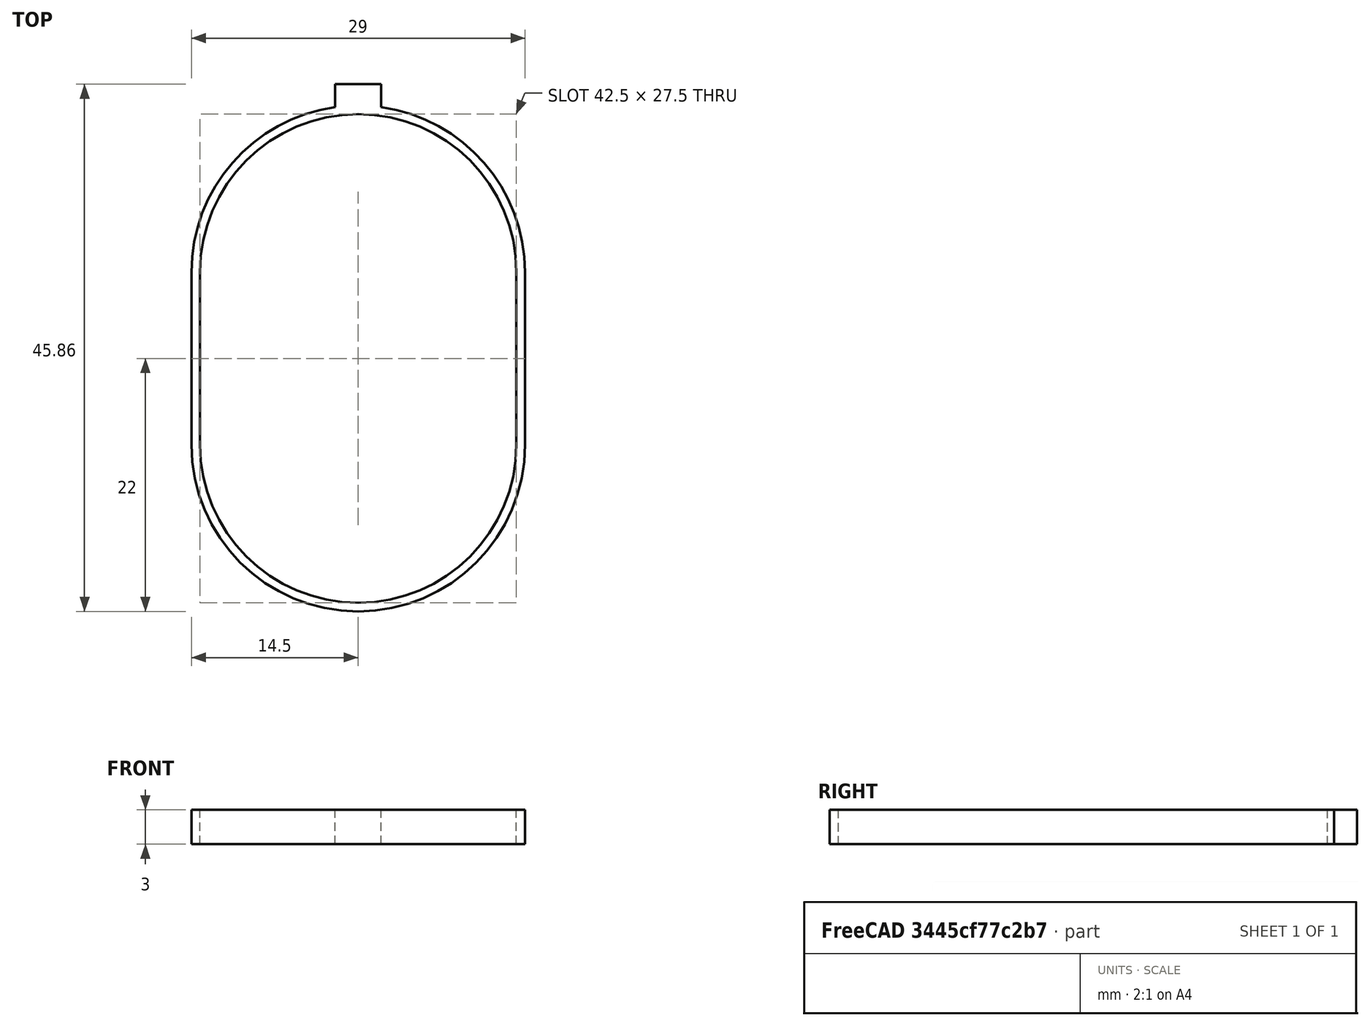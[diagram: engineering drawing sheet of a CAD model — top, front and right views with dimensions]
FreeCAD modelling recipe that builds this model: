
FCSTD DOCUMENT  (FreeCAD 0.19R)
Label: OTS-0005-00_zip-tie
License: All rights reserved
LicenseURL: http://en.wikipedia.org/wiki/All_rights_reserved
objects: Sketcher::SketchObject×1, PartDesign::Pad×1, PartDesign::Body×1
note: 4 computed .brp shape members not serialized (recipe doc carries the construction recipe); baked Part::Feature solids carry a one-line shape summary decoded from their .brp

FEATURE [Sketcher::SketchObject] Sketch
  FullyConstrained = true
  MapMode = 5
  Support = -> [XY_Plane]
  sketch-geometry (12):
    g0: ArcOfCircle CenterX=0 CenterY=-14.5 CenterZ=0 NormalX=0 NormalY=0 NormalZ=1 AngleXU=0 Radius=14.5 StartAngle=1.70917 EndAngle=3.14159
    g1: LineSegment StartX=2 StartY=-0.138593 StartZ=0 EndX=2 EndY=1.86141 EndZ=0
    g2: LineSegment StartX=2 StartY=1.86141 StartZ=0 EndX=-2 EndY=1.86141 EndZ=0
    g3: LineSegment StartX=-2 StartY=1.86141 StartZ=0 EndX=-2 EndY=-0.138593 EndZ=0
    g4: ArcOfCircle CenterX=0 CenterY=-14.5 CenterZ=0 NormalX=0 NormalY=0 NormalZ=1 AngleXU=0 Radius=13.75 StartAngle=7.87486e-07 EndAngle=3.14159
    g5: ArcOfCircle CenterX=0 CenterY=-14.5 CenterZ=0 NormalX=0 NormalY=0 NormalZ=1 AngleXU=0 Radius=14.5 StartAngle=2.61187e-06 EndAngle=1.43242
    g6: LineSegment StartX=-14.5 StartY=-14.5 StartZ=0 EndX=-14.5 EndY=-29.5 EndZ=0
    g7: LineSegment StartX=-13.75 StartY=-14.5 StartZ=0 EndX=-13.75 EndY=-29.5 EndZ=0
    g8: LineSegment StartX=13.75 StartY=-14.5 StartZ=0 EndX=13.75 EndY=-29.5 EndZ=0
    g9: LineSegment StartX=14.5 StartY=-14.5 StartZ=0 EndX=14.5 EndY=-29.5 EndZ=0
    g10: ArcOfCircle CenterX=0 CenterY=-29.5 CenterZ=0 NormalX=0 NormalY=0 NormalZ=1 AngleXU=0 Radius=13.75 StartAngle=3.14159 EndAngle=6.28319
    g11: ArcOfCircle CenterX=0 CenterY=-29.5 CenterZ=0 NormalX=0 NormalY=0 NormalZ=1 AngleXU=0 Radius=14.5 StartAngle=3.14159 EndAngle=6.28319
  constraints (37):
    c: PointOnObject(g0,g-2)
    c: PointOnObject(g-1,g0)
    c: Diameter(g0) = 29
    c: Coincident(g1,g2)
    c: Coincident(g2,g3)
    c: Vertical(g1)
    c: Vertical(g3)
    c: DistanceX(g2,g2) = 4
    c: DistanceY(g3,g3) = 2
    c: Coincident(g4,g0)
    c: Diameter(g4) = 27.5
    c: Coincident(g0,g3)
    c: Coincident(g1,g5)
    c: Symmetric(g2,g1,g-2)
    c: Equal(g0,g5)
    c: Coincident(g0,g5)
    c: Coincident(g6,g0)
    c: Coincident(g7,g4)
    c: Coincident(g8,g4)
    c: Coincident(g9,g5)
    c: PointOnObject(g10,g-2)
    c: Coincident(g11,g10)
    c: Coincident(g7,g10)
    c: Coincident(g8,g10)
    c: Coincident(g6,g11)
    c: Coincident(g9,g11)
    c: Tangent(g6,g0)
    c: Tangent(g7,g4)
    c: Tangent(g8,g4)
    c: Tangent(g9,g5)
    c: Tangent(g11,g9)
    c: Tangent(g11,g6)
    c: Tangent(g10,g7)
    c: Tangent(g10,g8)
    c: Vertical(g7)
    c: Vertical(g6)
    c: DistanceY(g10,g0) = 15
FEATURE [PartDesign::Pad] Pad
  Direction = (1,1,1)
  Length = 3
  Length2 = 100
  Profile = -> Sketch
  Type = 0
FEATURE [PartDesign::Body] Body
  Group = -> [Sketch,Pad]
  Origin = -> Origin
  Tip = -> Pad
